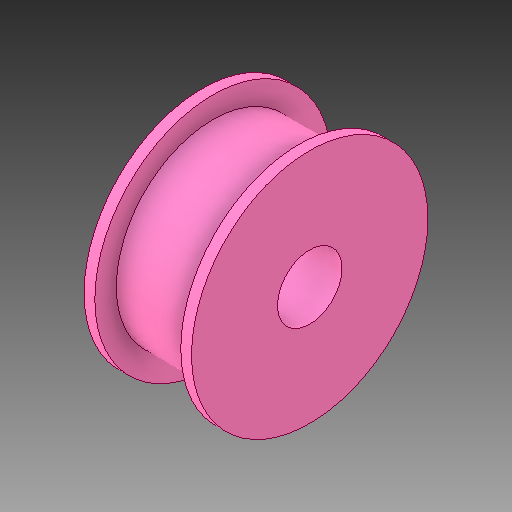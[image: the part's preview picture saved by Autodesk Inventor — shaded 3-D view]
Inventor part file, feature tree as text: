
AUTODESK INVENTOR PART (.ipt)
format: ipt  version: 2017 SP1 (Build 210196100, 196)  size: 142,848 bytes
history: native  units: in
note: dims shown in document units (in); Inventor stores cm internally (conversion verified against a paired STEP export)
features: extrude x4, sketch x4
ambient origin geometry x8: Origin, YZ Plane, XZ Plane, XY Plane, X Axis, Y Axis, Z Axis, Center Point
bodies: Solid1 (feature_tree)
feature tree (8):
  extrude  "Extrusion1"  Depth=0.375in
  extrude  "Extrusion2"  Depth=0.5in
  extrude  "Extrusion3"  Depth=0.0625in TaperAngle=0.0deg
  extrude  "Extrusion4"  Depth=0.1875in TaperAngle=0.0deg
  sketch  "Sketch1"  dims[d0=1.125in d2=0.375in]
  sketch  "Sketch2"  dims[d4=0.5in d5=0.0in d6=0.125in]
  sketch  "Sketch3"  dims[d7=0.0625in d8=0.0in d9=0.0625in d10=0.0in]
  sketch  "Sketch4"  dims[d11=0.1875in d12=0.375in d13=0.0in]
